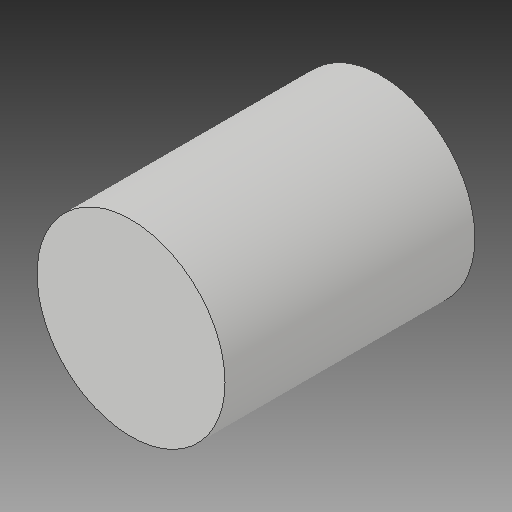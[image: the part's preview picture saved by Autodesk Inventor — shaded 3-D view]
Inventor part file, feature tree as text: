
AUTODESK INVENTOR PART (.ipt)
format: ipt  version: 2017 (Build 210142000, 142)  size: 90,112 bytes
history: native  units: in
note: dims shown in document units (in); Inventor stores cm internally (conversion verified against a paired STEP export)
features: extrude x1, sketch x1
ambient origin geometry x8: Origin, YZ Plane, XZ Plane, XY Plane, X Axis, Y Axis, Z Axis, Center Point
bodies: Solid1 (feature_tree)
feature tree (2):
  extrude  "Extrusion1"  Depth=0.25in TaperAngle=0.0deg
  sketch  "Sketch1"  dims[d0=0.188in d1=0.25in d2=0.0in]
